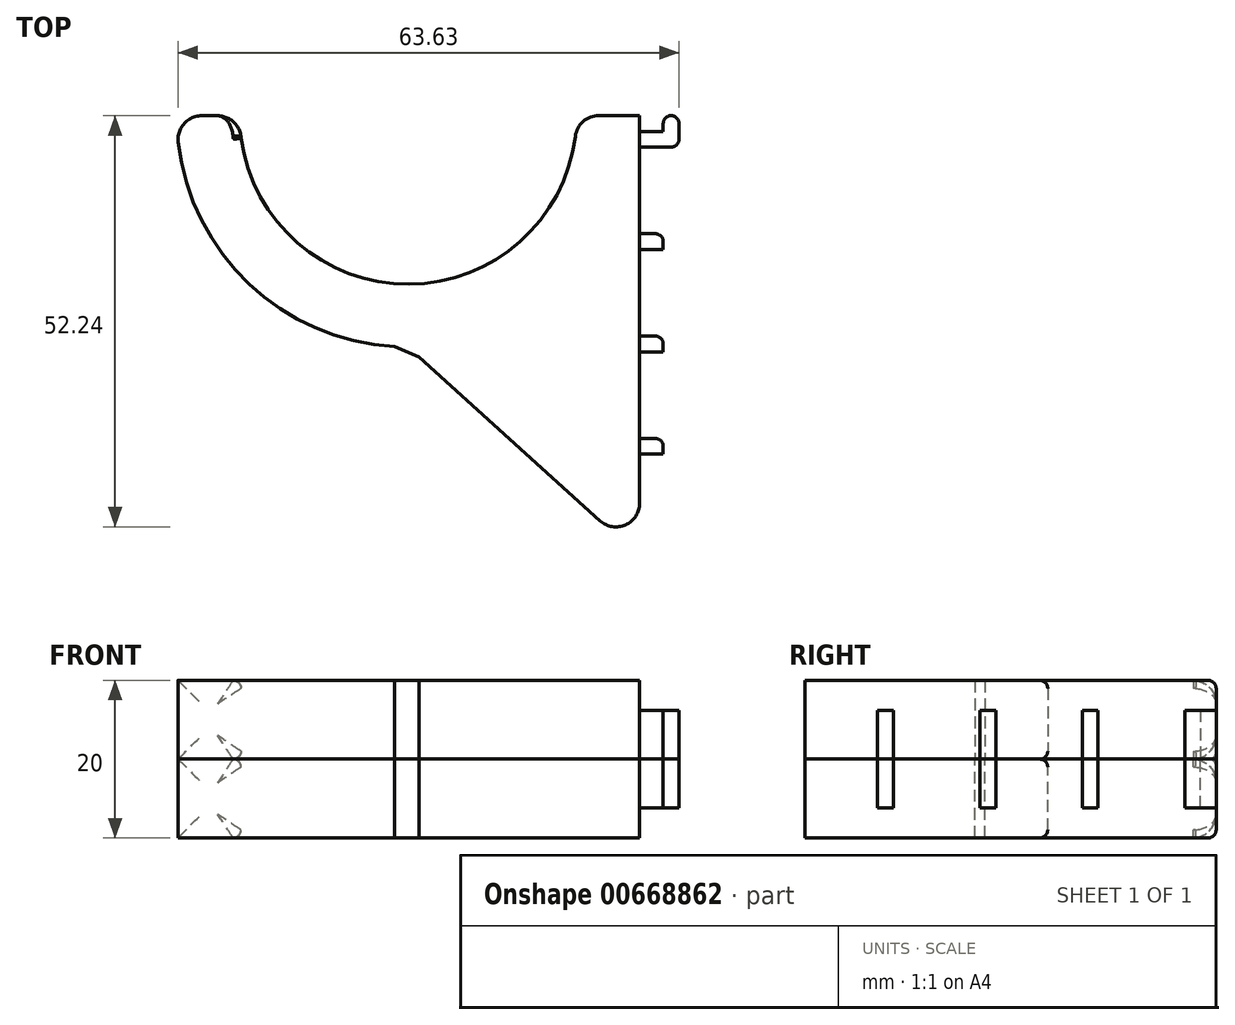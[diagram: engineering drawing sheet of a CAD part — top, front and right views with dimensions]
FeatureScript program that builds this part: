
annotation { "Feature Type Name" : "Feature", "Feature Type Description" : "" }
export const myFeature = defineFeature(function(context is Context, id is Id, definition is map)
    precondition{}
    {
        {
            var Q0;
            Q0=qCreatedBy(makeId("Top.planeOp"),FACE);
            var sketch = newSketch(context, id + "F0", { "sketchPlane" : qUnion([Q0])});
            skArc(sketch, "E0", {"start": v(-21.4, 29.4) * mm, "mid": v(0, 8) * mm, "end": v(21.4, 29.4) * mm});
            skLineSegment(sketch, "E1", {"start": v(-21.4, 29.4) * mm, "end": v(21.4, 29.4) * mm, "construction": true});
            skArc(sketch, "E2", {"start": v(-29.4, 29.4) * mm, "mid": v(0, 0) * mm, "end": v(29.4, 29.4) * mm});
            skLineSegment(sketch, "E3", {"start": v(-29.4, 29.4) * mm, "end": v(-21.4, 29.4) * mm});
            skLineSegment(sketch, "E4", {"start": v(29.4, 29.4) * mm, "end": v(29.4, -26.6) * mm});
            skLineSegment(sketch, "E5", {"start": v(29.4, -26.6) * mm, "end": v(0, 0) * mm});
            skLineSegment(sketch, "E6", {"start": v(21.4, 29.4) * mm, "end": v(29.4, 29.4) * mm});
            skSolve(sketch);
        }
        {
            var Q0;
            Q0=makeQuery(id+"F0.imprint","IMPRINT",FACE,{"disambiguationData":[TD([[makeQuery(id+"F0.imprint","IMPRINT",EDGE,{"derivedFrom":sQuery(id+"F0.wireOp",EDGE,"E0")}),-1.0]])]});
            var Q1;
            {var subQ0=sQuery(id+"F0.wireOp",EDGE,"E4");Q1=makeQuery(id+"F0.imprint","IMPRINT",FACE,{"disambiguationData":[TD([[makeQuery(id+"F0.imprint","IMPRINT",EDGE,{"derivedFrom":subQ0}),-1.0]])]});}
            extrude(context, id + "F1", {"entities" : qUnion([Q0, Q1]), "depth" : 10 * mm, "offsetDistance" : 25 * mm});
        }
        {
            var Q0;
            Q0=makeQuery(id+"F1.opExtrude","SWEPT_EDGE",EDGE,{"disambiguationData":[OSD([sQuery(id+"F0.wireOp",EDGE,"E2"),sQuery(id+"F0.wireOp",EDGE,"E5")])]});
            chamfer(context, id + "F2", {"entities" : qUnion([Q0]), "width" : 5 * mm, "tangentPropagation" : true});
        }
        {
            var Q0;
            Q0=makeQuery(id+"F1.opExtrude","SWEPT_FACE",FACE,{"disambiguationData":[OSD([sQuery(id+"F0.wireOp",EDGE,"E4")])]});
            var sketch = newSketch(context, id + "F3", { "sketchPlane" : qUnion([Q0])});
            skLineSegment(sketch, "E7.bottom", {"start": v(25.4, 6.2) * mm, "end": v(27.4, 6.2) * mm});
            skLineSegment(sketch, "E7.top", {"start": v(25.4, 0) * mm, "end": v(27.4, 0) * mm});
            skLineSegment(sketch, "E7.left", {"start": v(25.4, 6.2) * mm, "end": v(25.4, 0) * mm});
            skLineSegment(sketch, "E7.right", {"start": v(27.4, 6.2) * mm, "end": v(27.4, 0) * mm});
            skLineSegment(sketch, "E8.bottom", {"start": v(12.4, 6.2) * mm, "end": v(14.4, 6.2) * mm});
            skLineSegment(sketch, "E8.top", {"start": v(12.4, 0) * mm, "end": v(14.4, 0) * mm});
            skLineSegment(sketch, "E8.left", {"start": v(12.4, 6.2) * mm, "end": v(12.4, 0) * mm});
            skLineSegment(sketch, "E8.right", {"start": v(14.4, 6.2) * mm, "end": v(14.4, 0) * mm});
            skLineSegment(sketch, "E9.bottom", {"start": v(-0.6, 6.2) * mm, "end": v(1.4, 6.2) * mm});
            skLineSegment(sketch, "E9.top", {"start": v(-0.6, 0) * mm, "end": v(1.4, 0) * mm});
            skLineSegment(sketch, "E9.left", {"start": v(-0.6, 6.2) * mm, "end": v(-0.6, 0) * mm});
            skLineSegment(sketch, "E9.right", {"start": v(1.4, 6.2) * mm, "end": v(1.4, 0) * mm});
            skLineSegment(sketch, "E10.bottom", {"start": v(-13.6, 6.2) * mm, "end": v(-11.6, 6.2) * mm});
            skLineSegment(sketch, "E10.top", {"start": v(-13.6, 0) * mm, "end": v(-11.6, 0) * mm});
            skLineSegment(sketch, "E10.left", {"start": v(-13.6, 6.2) * mm, "end": v(-13.6, 0) * mm});
            skLineSegment(sketch, "E10.right", {"start": v(-11.6, 6.2) * mm, "end": v(-11.6, 0) * mm});
            skLineSegment(sketch, "E11", {"start": v(-11.6, 6.2) * mm, "end": v(-0.6, 6.2) * mm, "construction": true});
            skLineSegment(sketch, "E12", {"start": v(1.4, 6.2) * mm, "end": v(12.4, 6.2) * mm, "construction": true});
            skLineSegment(sketch, "E13", {"start": v(14.4, 6.2) * mm, "end": v(25.4, 6.2) * mm, "construction": true});
            skLineSegment(sketch, "E14", {"start": v(27.4, 6.2) * mm, "end": v(29.4, 6.2) * mm, "construction": true});
            skSolve(sketch);
        }
        {
            var Q0;
            Q0 = qSketchRegion(id + "F3", true);
            extrude(context, id + "F4", {"entities" : qUnion([Q0]), "operationType" : NewBodyOperationType.ADD, "depth" : 3 * mm, "offsetDistance" : 25 * mm});
        }
        {
            var Q0;
            Q0=makeQuery(id+"F4.opExtrude","SWEPT_FACE",FACE,{"disambiguationData":[OSD([sQuery(id+"F3.wireOp",EDGE,"E7.left")])]});
            var sketch = newSketch(context, id + "F5", { "sketchPlane" : qUnion([Q0])});
            skLineSegment(sketch, "E15.bottom", {"start": v(32.4, 6.2) * mm, "end": v(34.4, 6.2) * mm});
            skLineSegment(sketch, "E15.top", {"start": v(32.4, 0) * mm, "end": v(34.4, 0) * mm});
            skLineSegment(sketch, "E15.left", {"start": v(32.4, 6.2) * mm, "end": v(32.4, 0) * mm});
            skLineSegment(sketch, "E15.right", {"start": v(34.4, 6.2) * mm, "end": v(34.4, 0) * mm});
            skSolve(sketch);
        }
        {
            var Q0;
            Q0=makeQuery(id+"F5.imprint","IMPRINT",FACE,{"disambiguationData":[TD([[makeQuery(id+"F5.imprint","IMPRINT",EDGE,{"derivedFrom":sQuery(id+"F5.wireOp",EDGE,"E15.bottom")}),-1.0]])]});
            extrude(context, id + "F6", {"entities" : qUnion([Q0]), "operationType" : NewBodyOperationType.ADD, "oppositeDirection" : true, "depth" : 4 * mm, "offsetDistance" : 25 * mm});
        }
        {
            var Q0;
            Q0=makeQuery(id+"F6.opExtrude","CAP_EDGE",EDGE,{"disambiguationData":[OSD([sQuery(id+"F5.wireOp",EDGE,"E15.left")])],"isStart":false});
            var Q1;
            Q1=makeQuery(id+"F4.opExtrude","CAP_EDGE",EDGE,{"disambiguationData":[OSD([sQuery(id+"F3.wireOp",EDGE,"E7.right")])],"isStart":false});
            var Q2;
            Q2=makeQuery(id+"F6.opExtrude","CAP_EDGE",EDGE,{"disambiguationData":[OSD([sQuery(id+"F5.wireOp",EDGE,"E15.right")])],"isStart":true});
            var Q3;
            Q3=makeQuery(id+"F6.opExtrude","CAP_EDGE",EDGE,{"disambiguationData":[OSD([sQuery(id+"F5.wireOp",EDGE,"E15.right")])],"isStart":false});
            var Q4;
            Q4=makeQuery(id+"F4.opExtrude","CAP_EDGE",EDGE,{"disambiguationData":[OSD([sQuery(id+"F3.wireOp",EDGE,"E7.left")])],"isStart":true});
            var Q5;
            Q5=makeQuery(id+"F4.opExtrude","CAP_EDGE",EDGE,{"disambiguationData":[OSD([sQuery(id+"F3.wireOp",EDGE,"E8.left")])],"isStart":true});
            var Q6;
            Q6=makeQuery(id+"F4.opExtrude","CAP_EDGE",EDGE,{"disambiguationData":[OSD([sQuery(id+"F3.wireOp",EDGE,"E9.left")])],"isStart":true});
            var Q7;
            Q7=makeQuery(id+"F4.opExtrude","CAP_EDGE",EDGE,{"disambiguationData":[OSD([sQuery(id+"F3.wireOp",EDGE,"E10.left")])],"isStart":true});
            var Q8;
            Q8=makeQuery(id+"F4.opExtrude","CAP_EDGE",EDGE,{"disambiguationData":[OSD([sQuery(id+"F3.wireOp",EDGE,"E8.right")])],"isStart":false});
            var Q9;
            Q9=makeQuery(id+"F4.opExtrude","CAP_EDGE",EDGE,{"disambiguationData":[OSD([sQuery(id+"F3.wireOp",EDGE,"E9.right")])],"isStart":false});
            var Q10;
            Q10=makeQuery(id+"F4.opExtrude","CAP_EDGE",EDGE,{"disambiguationData":[OSD([sQuery(id+"F3.wireOp",EDGE,"E10.right")])],"isStart":false});
            var Q11;
            Q11=makeQuery(id+"F4.opExtrude","CAP_EDGE",EDGE,{"disambiguationData":[OSD([sQuery(id+"F3.wireOp",EDGE,"E8.right")])],"isStart":true});
            var Q12;
            Q12=makeQuery(id+"F4.opExtrude","CAP_EDGE",EDGE,{"disambiguationData":[OSD([sQuery(id+"F3.wireOp",EDGE,"E9.right")])],"isStart":true});
            var Q13;
            Q13=makeQuery(id+"F4.opExtrude","CAP_EDGE",EDGE,{"disambiguationData":[OSD([sQuery(id+"F3.wireOp",EDGE,"E10.right")])],"isStart":true});
            var Q14;
            Q14=makeQuery(id+"F4.opExtrude","CAP_EDGE",EDGE,{"disambiguationData":[OSD([sQuery(id+"F3.wireOp",EDGE,"E10.bottom")])],"isStart":true});
            var Q15;
            Q15=makeQuery(id+"F4.opExtrude","CAP_EDGE",EDGE,{"disambiguationData":[OSD([sQuery(id+"F3.wireOp",EDGE,"E9.bottom")])],"isStart":true});
            var Q16;
            Q16=makeQuery(id+"F4.opExtrude","CAP_EDGE",EDGE,{"disambiguationData":[OSD([sQuery(id+"F3.wireOp",EDGE,"E8.bottom")])],"isStart":true});
            var Q17;
            Q17=makeQuery(id+"F4.opExtrude","CAP_EDGE",EDGE,{"disambiguationData":[OSD([sQuery(id+"F3.wireOp",EDGE,"E7.bottom")])],"isStart":true});
            var Q18;
            Q18=makeQuery(id+"F4.opExtrude","CAP_EDGE",EDGE,{"disambiguationData":[OSD([sQuery(id+"F3.wireOp",EDGE,"E7.right")])],"isStart":true});
            fillet(context, id + "F7", {"entities" : qUnion([Q0, Q1, Q2, Q3, Q4, Q5, Q6, Q7, Q8, Q9, Q10, Q11, Q12, Q13, Q14, Q15, Q16, Q17, Q18]), "radius" : 1 * mm, "tangentPropagation" : true, "allowEdgeOverflow" : false});
        }
        {
            var Q0;
            Q0=makeQuery(id+"F1.opExtrude","SWEPT_EDGE",EDGE,{"disambiguationData":[OSD([sQuery(id+"F0.wireOp",EDGE,"E0"),sQuery(id+"F0.wireOp",EDGE,"E6")])]});
            var Q1;
            Q1=makeQuery(id+"F1.opExtrude","SWEPT_FACE",FACE,{"disambiguationData":[OSD([sQuery(id+"F0.wireOp",EDGE,"E3")])]});
            var Q2;
            Q2=makeQuery(id+"F1.opExtrude","SWEPT_EDGE",EDGE,{"disambiguationData":[OSD([sQuery(id+"F0.wireOp",EDGE,"E4"),sQuery(id+"F0.wireOp",EDGE,"E5")])]});
            fillet(context, id + "F8", {"entities" : qUnion([Q0, Q1, Q2]), "radius" : 3 * mm, "tangentPropagation" : true, "allowEdgeOverflow" : false});
        }
        {
            var Q0;
            Q0=makeQuery(id+"F1.opExtrude","CAP_EDGE",EDGE,{"disambiguationData":[OSD([sQuery(id+"F0.wireOp",EDGE,"E0")])],"isStart":false});
            var Q1;
            Q1=makeQuery(id+"F1.opExtrude","CAP_EDGE",EDGE,{"disambiguationData":[OSD([sQuery(id+"F0.wireOp",EDGE,"E0")])],"isStart":true});
            fillet(context, id + "F9", {"entities" : qUnion([Q0, Q1]), "radius" : 1 * mm, "tangentPropagation" : true, "allowEdgeOverflow" : false});
        }
        {
            var Q0;
            Q0=makeQuery(id+"F1.opExtrude","SWEPT_BODY",BODY,{"disambiguationData":[OSD([sQuery(id+"F0.wireOp",EDGE,"E0"),sQuery(id+"F0.wireOp",EDGE,"E2"),sQuery(id+"F0.wireOp",EDGE,"E3"),sQuery(id+"F0.wireOp",EDGE,"E4"),sQuery(id+"F0.wireOp",EDGE,"E5"),sQuery(id+"F0.wireOp",EDGE,"E6")])]});
            var Q1;
            Q1=qCreatedBy(makeId("Top.planeOp"),FACE);
            mirror(context, id + "F10", {"entities" : qUnion([Q0]), "mirrorPlane" : qUnion([Q1])});
        }
    });
